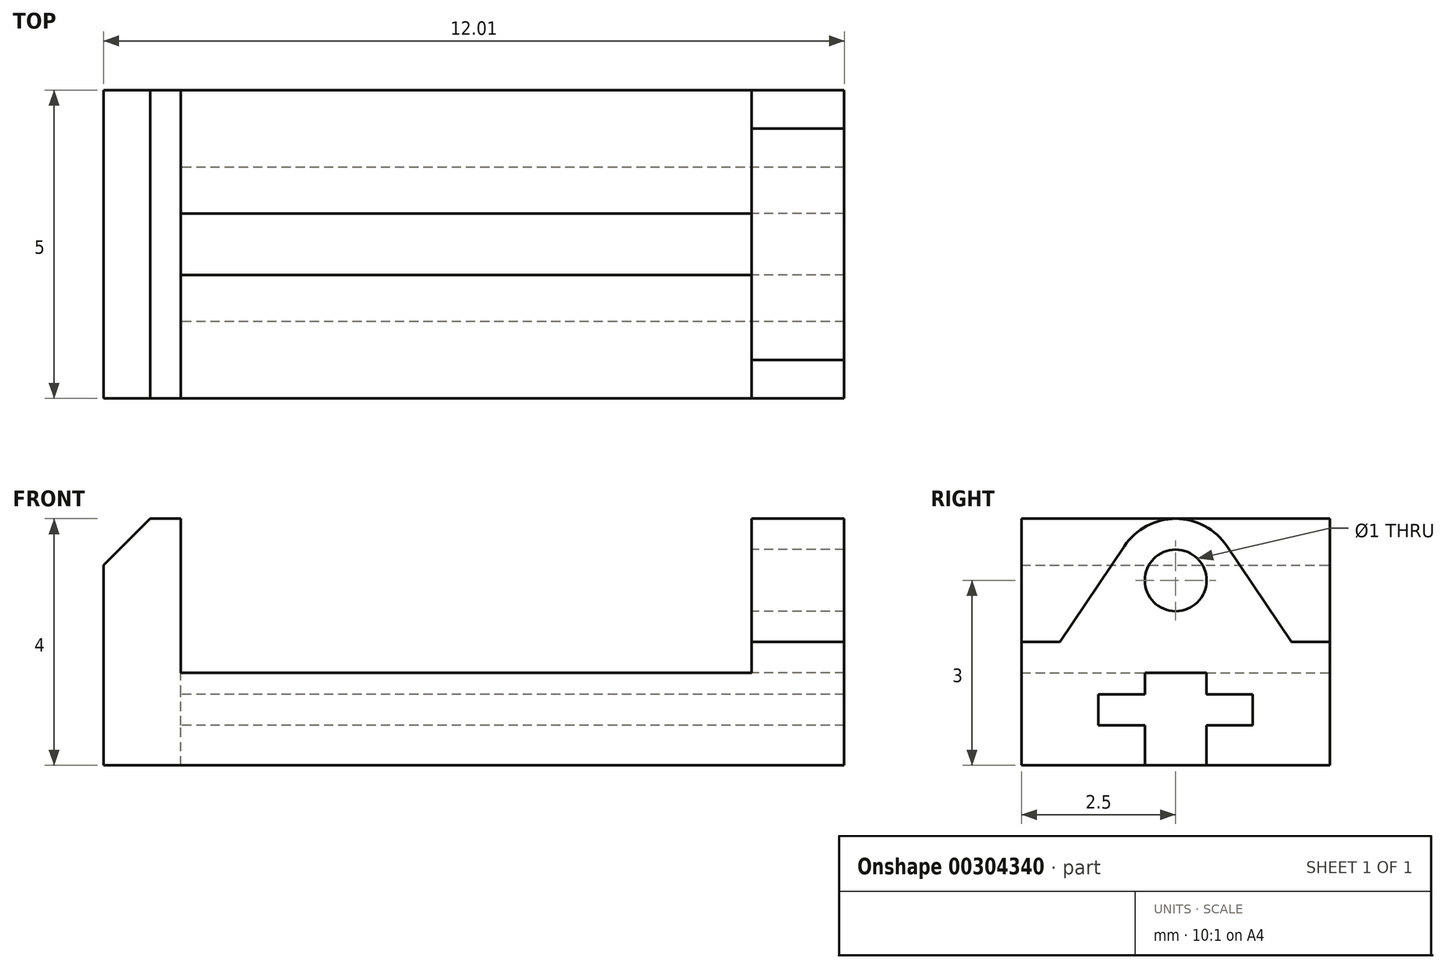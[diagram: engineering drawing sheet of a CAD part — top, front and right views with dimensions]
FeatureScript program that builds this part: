
annotation { "Feature Type Name" : "Feature", "Feature Type Description" : "" }
export const myFeature = defineFeature(function(context is Context, id is Id, definition is map)
    precondition{}
    {
        {
            var Q0;
            Q0=qCreatedBy(makeId("Right.planeOp"),FACE);
            var sketch = newSketch(context, id + "F0", { "sketchPlane" : qUnion([Q0])});
            skLineSegment(sketch, "E0.bottom", {"start": v(0, 0) * mm, "end": v(5, 0) * mm});
            skLineSegment(sketch, "E0.top", {"start": v(0, 1.5) * mm, "end": v(5, 1.5) * mm});
            skLineSegment(sketch, "E0.left", {"start": v(0, 0) * mm, "end": v(0, 1.5) * mm});
            skLineSegment(sketch, "E0.right", {"start": v(5, 0) * mm, "end": v(5, 1.5) * mm});
            skLineSegment(sketch, "E1", {"start": v(2, 0) * mm, "end": v(2, 0.65) * mm});
            skLineSegment(sketch, "E2", {"start": v(2, 0.65) * mm, "end": v(1.25, 0.65) * mm});
            skLineSegment(sketch, "E3", {"start": v(1.25, 0.65) * mm, "end": v(1.25, 1.15) * mm});
            skLineSegment(sketch, "E4", {"start": v(1.25, 1.15) * mm, "end": v(2, 1.15) * mm});
            skLineSegment(sketch, "E5", {"start": v(2, 1.15) * mm, "end": v(2, 1.5) * mm});
            skLineSegment(sketch, "E6", {"start": v(3, 1.5) * mm, "end": v(3, 1.15) * mm});
            skLineSegment(sketch, "E7", {"start": v(3, 1.15) * mm, "end": v(3.75, 1.15) * mm});
            skLineSegment(sketch, "E8", {"start": v(3.75, 1.15) * mm, "end": v(3.75, 0.65) * mm});
            skLineSegment(sketch, "E9", {"start": v(3.75, 0.65) * mm, "end": v(3, 0.65) * mm});
            skLineSegment(sketch, "E10", {"start": v(3, 0.65) * mm, "end": v(3, 0) * mm});
            skLineSegment(sketch, "E11", {"start": v(2.5, 1.5) * mm, "end": v(2.5, 0) * mm, "construction": true});
            skSolve(sketch);
        }
        {
            var Q0;
            Q0=makeQuery(id+"F0.imprint","IMPRINT",FACE,{"disambiguationData":[TD([[makeQuery(id+"F0.imprint","IMPRINT",EDGE,{"derivedFrom":sQuery(id+"F0.wireOp",EDGE,"E0.top")}),-1.0]])]});
            extrude(context, id + "F1", {"entities" : qUnion([Q0]), "endBound" : BoundingType.SYMMETRIC, "depth" : 9.25 * mm});
        }
        {
            var Q0;
            Q0=makeQuery(id+"F1.opExtrude","CAP_FACE",FACE,{"disambiguationData":[OSD([sQuery(id+"F0.wireOp",EDGE,"E0.bottom"),sQuery(id+"F0.wireOp",EDGE,"E0.top"),sQuery(id+"F0.wireOp",EDGE,"E0.left"),sQuery(id+"F0.wireOp",EDGE,"E1"),sQuery(id+"F0.wireOp",EDGE,"E2"),sQuery(id+"F0.wireOp",EDGE,"E3"),sQuery(id+"F0.wireOp",EDGE,"E4"),sQuery(id+"F0.wireOp",EDGE,"E5")])],"isStart":false});
            var sketch = newSketch(context, id + "F2", { "sketchPlane" : qUnion([Q0])});
            skLineSegment(sketch, "E12.bottom", {"start": v(0, 0) * mm, "end": v(5, 0) * mm});
            skLineSegment(sketch, "E12.top", {"start": v(0, 2) * mm, "end": v(0.63, 2) * mm});
            skLineSegment(sketch, "E12.left", {"start": v(0, 0) * mm, "end": v(0, 2) * mm});
            skLineSegment(sketch, "E12.right", {"start": v(5, 0) * mm, "end": v(5, 2) * mm});
            skLineSegment(sketch, "E13", {"start": v(2, 1.15) * mm, "end": v(2, 1.5) * mm});
            skLineSegment(sketch, "E14", {"start": v(2, 0) * mm, "end": v(2, 0.65) * mm});
            skLineSegment(sketch, "E15", {"start": v(2, 0.65) * mm, "end": v(1.25, 0.65) * mm});
            skLineSegment(sketch, "E16", {"start": v(1.25, 0.65) * mm, "end": v(1.25, 1.15) * mm});
            skLineSegment(sketch, "E17", {"start": v(1.25, 1.15) * mm, "end": v(2, 1.15) * mm});
            skPoint(sketch, "E18.0", {"position": v(3, 0) * mm});
            skPoint(sketch, "E19.0", {"position": v(3, 0.65) * mm});
            skPoint(sketch, "E20.0", {"position": v(3.75, 0.65) * mm});
            skPoint(sketch, "E21.0", {"position": v(3.75, 1.15) * mm});
            skPoint(sketch, "E22.0", {"position": v(3, 1.15) * mm});
            skLineSegment(sketch, "E23", {"start": v(3, 0) * mm, "end": v(3, 0.65) * mm});
            skLineSegment(sketch, "E24", {"start": v(3.75, 0.65) * mm, "end": v(3.75, 1.15) * mm});
            skLineSegment(sketch, "E25", {"start": v(3, 1.15) * mm, "end": v(3, 1.5) * mm});
            skLineSegment(sketch, "E26", {"start": v(3, 1.15) * mm, "end": v(3.75, 1.15) * mm});
            skLineSegment(sketch, "E27", {"start": v(3.75, 0.65) * mm, "end": v(3, 0.65) * mm});
            skLineSegment(sketch, "E28", {"start": v(0.63, 2) * mm, "end": v(1.67, 3.56) * mm});
            skLineSegment(sketch, "E29", {"start": v(4.37, 2) * mm, "end": v(3.33, 3.56) * mm});
            skArc(sketch, "E30", {"start": v(3.33, 3.56) * mm, "mid": v(2.5, 4) * mm, "end": v(1.67, 3.56) * mm});
            skCircle(sketch, "E31", {"center": v(2.5, 3) * mm, "radius": 0.5 * mm});
            skLineSegment(sketch, "E32", {"start": v(2, 1.5) * mm, "end": v(3, 1.5) * mm});
            skLineSegment(sketch, "E33.trimOffspring", {"start": v(4.38, 2) * mm, "end": v(5, 2) * mm});
            skSolve(sketch);
        }
        {
            var Q0;
            {var subQ0=sQuery(id+"F2.wireOp",EDGE,"E12.right");Q0=makeQuery(id+"F2.imprint","IMPRINT",FACE,{"disambiguationData":[TD([[makeQuery(id+"F2.imprint","IMPRINT",EDGE,{"derivedFrom":subQ0}),1.0]])]});}
            var Q1;
            {var subQ4=sQuery(id+"F2.wireOp",EDGE,"E14");Q1=makeQuery(id+"F2.imprint","IMPRINT",FACE,{"disambiguationData":[TD([[makeQuery(id+"F2.imprint","IMPRINT",EDGE,{"derivedFrom":subQ4}),1.0]])]});}
            var Q2;
            {var subQ5=sQuery(id+"F0.wireOp",EDGE,"E0.top");var subQ6=makeQuery(id+"F1.opExtrude","CAP_EDGE",EDGE,{"disambiguationData":[OSD([subQ5]),TDD([makeQuery(id+"F0.imprint","IMPRINT",EDGE,{"disambiguationData":[TD([[makeQuery(id+"F0.imprint","INTERSECT",VERTEX,{"derivedFrom":[subQ5,sQuery(id+"F0.wireOp",EDGE,"E0.left")]}),-1.0]])],"derivedFrom":subQ5})])],"isStart":false});Q2=makeQuery(id+"F2.imprint","IMPRINT",FACE,{"disambiguationData":[TD([[makeQuery(id+"F2.imprint","IMPRINT",EDGE,{"derivedFrom":subQ6}),1.0]])]});}
            extrude(context, id + "F3", {"entities" : qUnion([Q0, Q1, Q2]), "operationType" : NewBodyOperationType.ADD, "depth" : 1.5 * mm});
        }
        {
            var Q0;
            Q0=makeQuery(id+"F1.opExtrude","CAP_FACE",FACE,{"disambiguationData":[OSD([sQuery(id+"F0.wireOp",EDGE,"E0.bottom"),sQuery(id+"F0.wireOp",EDGE,"E0.top"),sQuery(id+"F0.wireOp",EDGE,"E0.left"),sQuery(id+"F0.wireOp",EDGE,"E1"),sQuery(id+"F0.wireOp",EDGE,"E2"),sQuery(id+"F0.wireOp",EDGE,"E3"),sQuery(id+"F0.wireOp",EDGE,"E4"),sQuery(id+"F0.wireOp",EDGE,"E5")])],"isStart":true});
            var sketch = newSketch(context, id + "F4", { "sketchPlane" : qUnion([Q0])});
            skPoint(sketch, "E34.0", {"position": v(-5, 0) * mm});
            skLineSegment(sketch, "E35.0", {"start": v(-5, 0) * mm, "end": v(-5, 1.5) * mm});
            skLineSegment(sketch, "E36", {"start": v(0, 0) * mm, "end": v(0, 4) * mm});
            skLineSegment(sketch, "E37", {"start": v(0, 4) * mm, "end": v(-5, 4) * mm});
            skLineSegment(sketch, "E38", {"start": v(-5, 4) * mm, "end": v(-5, 0) * mm});
            skLineSegment(sketch, "E39", {"start": v(-5, 0) * mm, "end": v(0, 0) * mm});
            skSolve(sketch);
        }
        {
            var Q0;
            Q0 = qSketchRegion(id + "F4", true);
            extrude(context, id + "F5", {"entities" : qUnion([Q0]), "operationType" : NewBodyOperationType.ADD, "depth" : 1.25 * mm});
        }
        {
            var Q0;
            Q0=makeQuery(id+"F5.opExtrude","CAP_EDGE",EDGE,{"disambiguationData":[OSD([sQuery(id+"F4.wireOp",EDGE,"E37")])],"isStart":false});
            chamfer(context, id + "F6", {"entities" : qUnion([Q0]), "chamferType" : ChamferType.OFFSET_ANGLE, "width" : .75 * mm, "oppositeDirection" : false, "angle" : 45 * degree, "tangentPropagation" : true});
        }
    });
